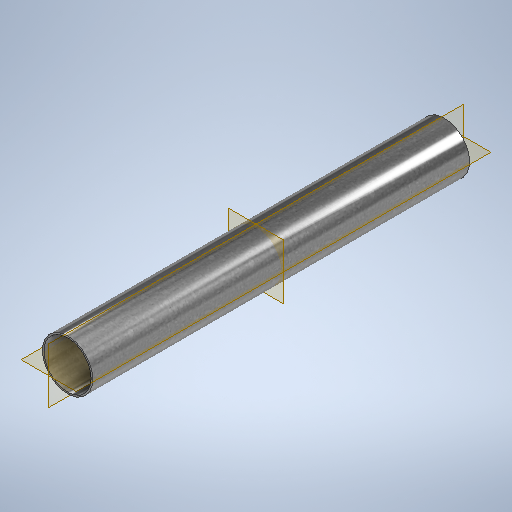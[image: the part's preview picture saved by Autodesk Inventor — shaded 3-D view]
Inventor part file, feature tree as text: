
AUTODESK INVENTOR PART (.ipt)
format: ipt  version: 2025.2 (Build 292293000, 293)  size: 287,744 bytes
history: native  units: mm
features: extrude x1, sketch x1
ambient origin geometry x8: Origin, YZ Plane, XZ Plane, XY Plane, X Axis, Y Axis, Z Axis, Center Point
bodies: Body1 (feature_tree)
feature tree (2):
  extrude  "Extrusão1"  Depth=750.0mm
  sketch  "Esboço2"  dims[d6=100.0mm d7=3.0mm d8=750.0mm d9=0.0mm]
